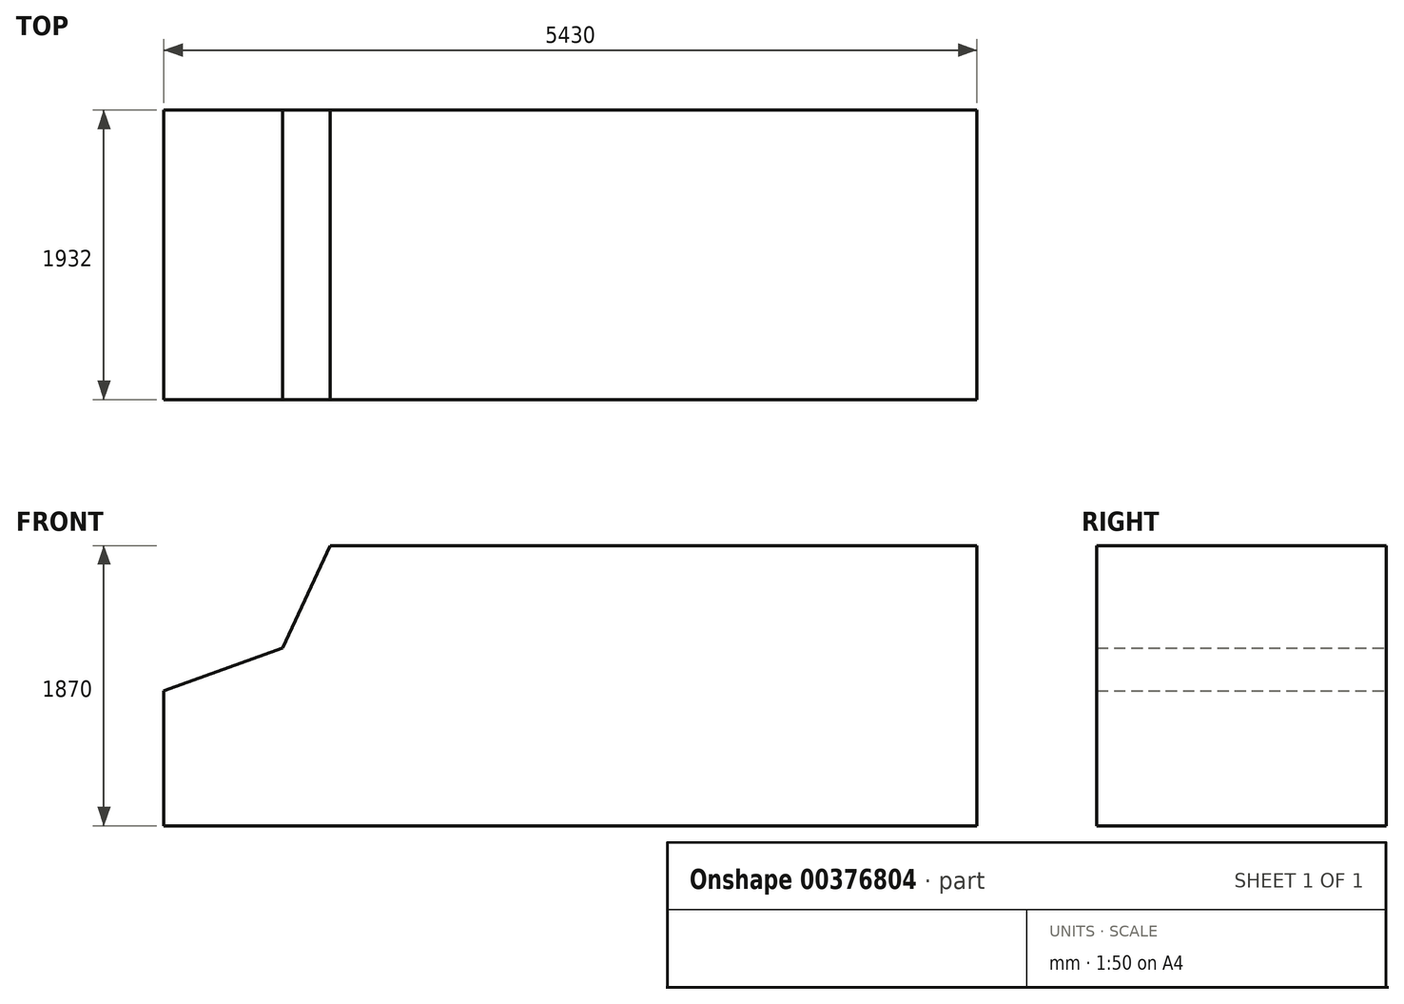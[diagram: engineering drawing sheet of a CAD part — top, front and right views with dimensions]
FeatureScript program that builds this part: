
annotation { "Feature Type Name" : "Feature", "Feature Type Description" : "" }
export const myFeature = defineFeature(function(context is Context, id is Id, definition is map)
    precondition{}
    {
        {
            var Q0;
            Q0=qCreatedBy(makeId("Front.planeOp"),FACE);
            var sketch = newSketch(context, id + "F0", { "sketchPlane" : qUnion([Q0])});
            skLineSegment(sketch, "E0", {"start": v(-2715, 0) * mm, "end": v(2715, 0) * mm});
            skLineSegment(sketch, "E1", {"start": v(-2715, 0) * mm, "end": v(-2715, 900) * mm});
            skLineSegment(sketch, "E2", {"start": v(-2715, 900) * mm, "end": v(-1922.88, 1188.3) * mm});
            skLineSegment(sketch, "E3", {"start": v(-405, 1870) * mm, "end": v(2715, 1870) * mm});
            skLineSegment(sketch, "E4", {"start": v(2715, 1870) * mm, "end": v(2715, 0) * mm});
            skLineSegment(sketch, "E5", {"start": v(-405, 1870) * mm, "end": v(-1605, 1870) * mm});
            skLineSegment(sketch, "E6", {"start": v(-1605, 1870) * mm, "end": v(-1922.88, 1188.3) * mm});
            skSolve(sketch);
        }
        {
            var Q0;
            Q0=makeQuery(id+"F0.imprint","IMPRINT",FACE,{"disambiguationData":[TD([[makeQuery(id+"F0.imprint","IMPRINT",EDGE,{"derivedFrom":sQuery(id+"F0.wireOp",EDGE,"E0")}),1.0]])]});
            extrude(context, id + "F1", {"entities" : qUnion([Q0]), "endBound" : BoundingType.SYMMETRIC, "depth" : 1932 * mm});
        }
    });
